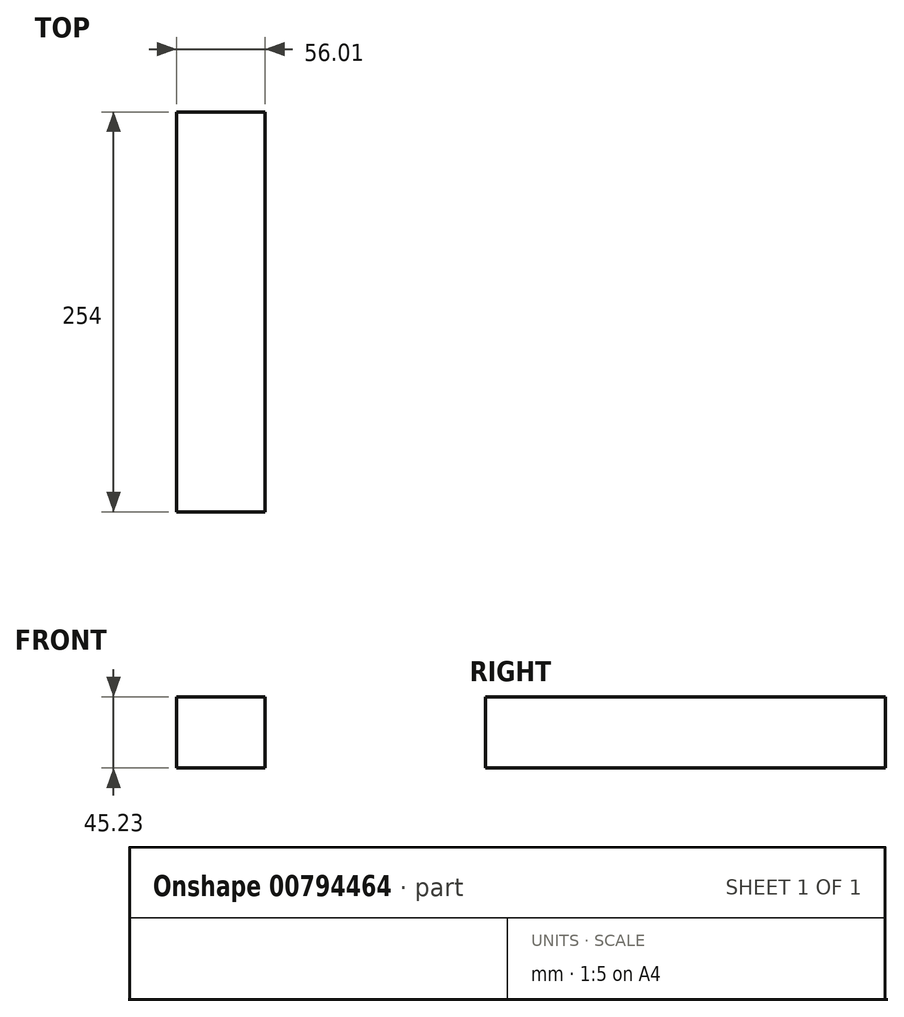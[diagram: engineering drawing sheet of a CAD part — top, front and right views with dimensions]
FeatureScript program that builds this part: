
annotation { "Feature Type Name" : "Feature", "Feature Type Description" : "" }
export const myFeature = defineFeature(function(context is Context, id is Id, definition is map)
    precondition{}
    {
        {
            var Q0;
            Q0=qCreatedBy(makeId("Front.planeOp"),FACE);
            var sketch = newSketch(context, id + "F0", { "sketchPlane" : qUnion([Q0])});
            skLineSegment(sketch, "E0.bottom", {"start": v(0, 0) * mm, "end": v(56.01, 0) * mm});
            skLineSegment(sketch, "E0.top", {"start": v(0, 45.23) * mm, "end": v(56.01, 45.23) * mm});
            skLineSegment(sketch, "E0.left", {"start": v(0, 0) * mm, "end": v(0, 45.23) * mm});
            skLineSegment(sketch, "E0.right", {"start": v(56.01, 0) * mm, "end": v(56.01, 45.23) * mm});
            skSolve(sketch);
        }
        {
            var Q0;
            Q0=makeQuery(id+"F0.imprint","IMPRINT",FACE,{"disambiguationData":[TD([[makeQuery(id+"F0.imprint","IMPRINT",EDGE,{"derivedFrom":sQuery(id+"F0.wireOp",EDGE,"E0.bottom")}),1.0]])]});
            extrude(context, id + "F1", {"entities" : qUnion([Q0]), "depth" : 254 * mm, "offsetDistance" : 25.4 * mm});
        }
    });
